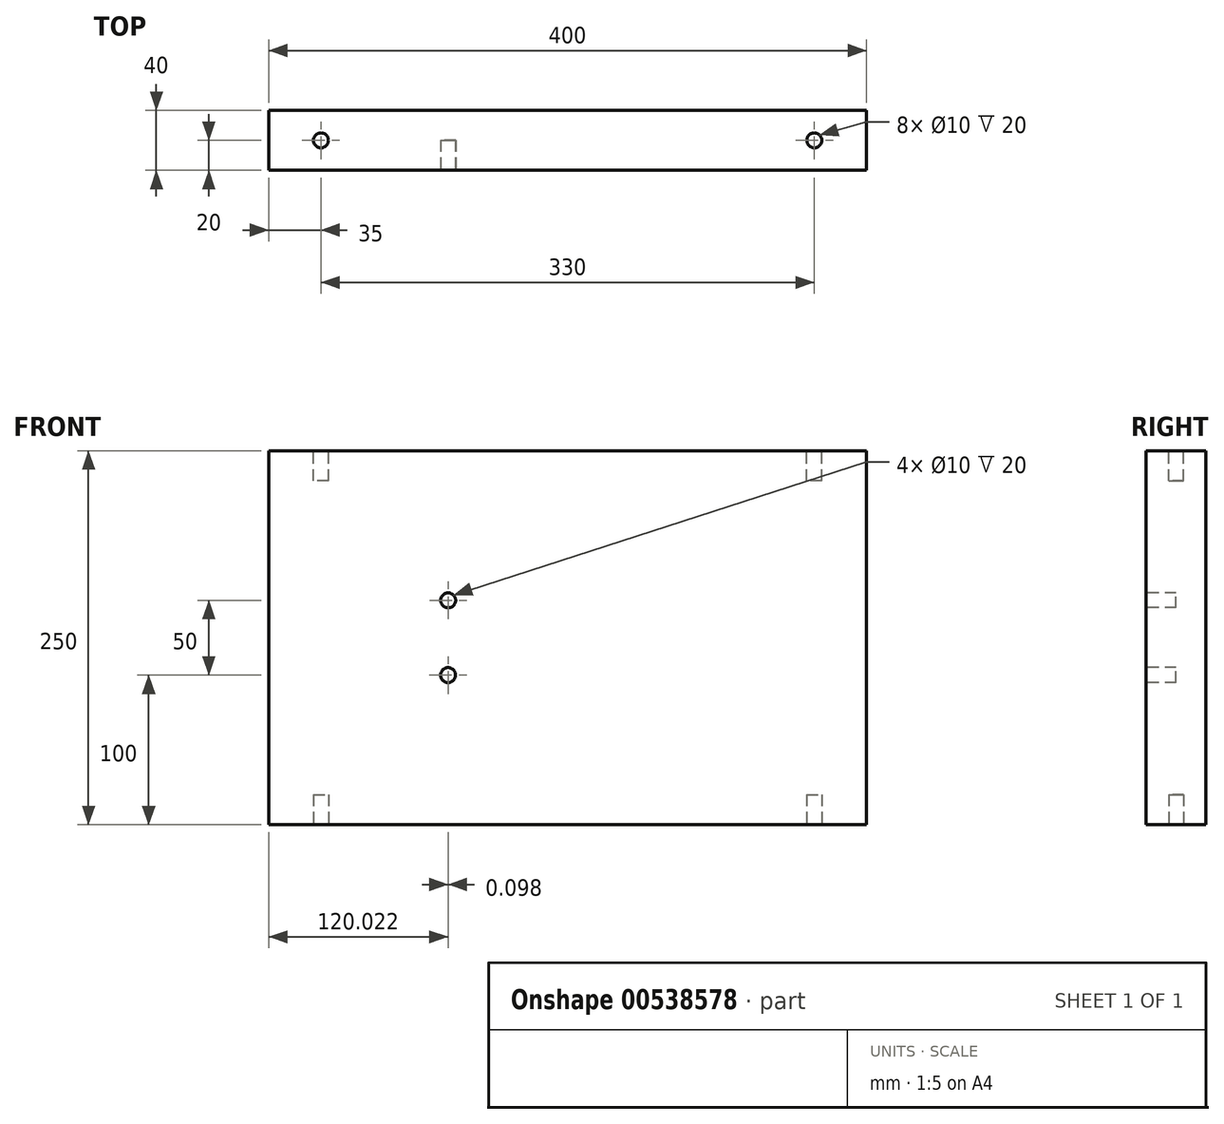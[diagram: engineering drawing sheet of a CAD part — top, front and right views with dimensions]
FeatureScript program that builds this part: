
annotation { "Feature Type Name" : "Feature", "Feature Type Description" : "" }
export const myFeature = defineFeature(function(context is Context, id is Id, definition is map)
    precondition{}
    {
        {
            var Q0;
            Q0=qCreatedBy(makeId("Right.planeOp"),FACE);
            var sketch = newSketch(context, id + "F0", { "sketchPlane" : qUnion([Q0])});
            skLineSegment(sketch, "E0.bottom", {"start": v(0, 0) * mm, "end": v(40, 0) * mm});
            skLineSegment(sketch, "E0.top", {"start": v(0, 250) * mm, "end": v(40, 250) * mm});
            skLineSegment(sketch, "E0.left", {"start": v(0, 0) * mm, "end": v(0, 250) * mm});
            skLineSegment(sketch, "E0.right", {"start": v(40, 0) * mm, "end": v(40, 250) * mm});
            skSolve(sketch);
        }
        {
            var Q0;
            Q0 = qSketchRegion(id + "F0", true);
            extrude(context, id + "F1", {"entities" : qUnion([Q0]), "endBound" : BoundingType.SYMMETRIC, "oppositeDirection" : true, "depth" : 400 * mm, "offsetDistance" : 25 * mm});
        }
        {
            var Q0;
            Q0=makeQuery(id+"F1.opExtrude","SWEPT_FACE",FACE,{"disambiguationData":[OSD([sQuery(id+"F0.wireOp",EDGE,"E0.left")])]});
            var sketch = newSketch(context, id + "F2", { "sketchPlane" : qUnion([Q0])});
            skLineSegment(sketch, "E1", {"start": v(-80, 250) * mm, "end": v(-80, 0) * mm, "construction": true});
            skSolve(sketch);
        }
        {
            var Q0;
            {var subQ0=sQuery(id+"F0.wireOp",EDGE,"E0.left");Q0=makeQuery(id+"F2.imprint","IMPRINT",FACE,{"disambiguationData":[TD([[makeQuery(id+"F2.imprint","IMPRINT",EDGE,{"derivedFrom":makeQuery(id+"F1.opExtrude","CAP_EDGE",EDGE,{"disambiguationData":[OSD([subQ0])],"isStart":true})}),1.0]])]});}
            var sketch = newSketch(context, id + "F3", { "sketchPlane" : qUnion([Q0])});
            skCircle(sketch, "E2", {"center": v(-79.88, 150) * mm, "radius": 5 * mm});
            skSolve(sketch);
        }
        {
            var Q0;
            {var subQ0=sQuery(id+"F0.wireOp",EDGE,"E0.left");Q0=makeQuery(id+"F2.imprint","IMPRINT",FACE,{"disambiguationData":[TD([[makeQuery(id+"F2.imprint","IMPRINT",EDGE,{"derivedFrom":makeQuery(id+"F1.opExtrude","CAP_EDGE",EDGE,{"disambiguationData":[OSD([subQ0])],"isStart":true})}),1.0]])]});}
            var sketch = newSketch(context, id + "F4", { "sketchPlane" : qUnion([Q0])});
            skCircle(sketch, "E3", {"center": v(-79.98, 100) * mm, "radius": 5 * mm});
            skSolve(sketch);
        }
        {
            var Q0;
            Q0=makeQuery(id+"F4.imprint","IMPRINT",FACE,{"disambiguationData":[TD([[makeQuery(id+"F4.imprint","IMPRINT",EDGE,{"derivedFrom":sQuery(id+"F4.wireOp",EDGE,"E3")}),1.0]])]});
            extrude(context, id + "F5", {"entities" : qUnion([Q0]), "operationType" : NewBodyOperationType.REMOVE, "oppositeDirection" : true, "depth" : 20 * mm, "offsetDistance" : 25 * mm});
        }
        {
            var Q0;
            Q0=makeQuery(id+"F3.imprint","IMPRINT",FACE,{"disambiguationData":[TD([[makeQuery(id+"F3.imprint","IMPRINT",EDGE,{"derivedFrom":sQuery(id+"F3.wireOp",EDGE,"E2")}),1.0]])]});
            extrude(context, id + "F6", {"entities" : qUnion([Q0]), "operationType" : NewBodyOperationType.REMOVE, "oppositeDirection" : true, "depth" : 20 * mm, "offsetDistance" : 25 * mm});
        }
        {
            var Q0;
            Q0=makeQuery(id+"F1.opExtrude","SWEPT_FACE",FACE,{"disambiguationData":[OSD([sQuery(id+"F0.wireOp",EDGE,"E0.top")])]});
            var sketch = newSketch(context, id + "F7", { "sketchPlane" : qUnion([Q0])});
            skCircle(sketch, "E4", {"center": v(-165, 20) * mm, "radius": 5 * mm});
            skSolve(sketch);
        }
        {
            var Q0;
            Q0=makeQuery(id+"F7.imprint","IMPRINT",FACE,{"disambiguationData":[TD([[makeQuery(id+"F7.imprint","IMPRINT",EDGE,{"derivedFrom":sQuery(id+"F7.wireOp",EDGE,"E4")}),1.0]])]});
            extrude(context, id + "F8", {"entities" : qUnion([Q0]), "operationType" : NewBodyOperationType.REMOVE, "oppositeDirection" : true, "depth" : 20 * mm, "offsetDistance" : 25 * mm});
        }
        {
            var Q0;
            Q0=makeQuery(id+"F1.opExtrude","SWEPT_FACE",FACE,{"disambiguationData":[OSD([sQuery(id+"F0.wireOp",EDGE,"E0.top")])]});
            var sketch = newSketch(context, id + "F9", { "sketchPlane" : qUnion([Q0])});
            skCircle(sketch, "E5", {"center": v(165, 20) * mm, "radius": 5 * mm});
            skSolve(sketch);
        }
        {
            var Q0;
            Q0=makeQuery(id+"F9.imprint","IMPRINT",FACE,{"disambiguationData":[TD([[makeQuery(id+"F9.imprint","IMPRINT",EDGE,{"derivedFrom":sQuery(id+"F9.wireOp",EDGE,"E5")}),1.0]])]});
            extrude(context, id + "F10", {"entities" : qUnion([Q0]), "operationType" : NewBodyOperationType.REMOVE, "oppositeDirection" : true, "depth" : 20 * mm, "offsetDistance" : 25 * mm});
        }
        {
            var Q0;
            Q0=makeQuery(id+"F1.opExtrude","SWEPT_FACE",FACE,{"disambiguationData":[OSD([sQuery(id+"F0.wireOp",EDGE,"E0.bottom")])]});
            var sketch = newSketch(context, id + "F11", { "sketchPlane" : qUnion([Q0])});
            skCircle(sketch, "E6", {"center": v(-165, -20) * mm, "radius": 5 * mm});
            skSolve(sketch);
        }
        {
            var Q0;
            Q0=makeQuery(id+"F11.imprint","IMPRINT",FACE,{"disambiguationData":[TD([[makeQuery(id+"F11.imprint","IMPRINT",EDGE,{"derivedFrom":sQuery(id+"F11.wireOp",EDGE,"E6")}),1.0]])]});
            extrude(context, id + "F12", {"entities" : qUnion([Q0]), "operationType" : NewBodyOperationType.REMOVE, "oppositeDirection" : true, "depth" : 20 * mm, "offsetDistance" : 25 * mm});
        }
        {
            var Q0;
            Q0=makeQuery(id+"F1.opExtrude","SWEPT_FACE",FACE,{"disambiguationData":[OSD([sQuery(id+"F0.wireOp",EDGE,"E0.bottom")])]});
            var sketch = newSketch(context, id + "F13", { "sketchPlane" : qUnion([Q0])});
            skCircle(sketch, "E7", {"center": v(165, -20) * mm, "radius": 5 * mm});
            skSolve(sketch);
        }
        {
            var Q0;
            Q0=makeQuery(id+"F13.imprint","IMPRINT",FACE,{"disambiguationData":[TD([[makeQuery(id+"F13.imprint","IMPRINT",EDGE,{"derivedFrom":sQuery(id+"F13.wireOp",EDGE,"E7")}),1.0]])]});
            extrude(context, id + "F14", {"entities" : qUnion([Q0]), "operationType" : NewBodyOperationType.REMOVE, "oppositeDirection" : true, "depth" : 20 * mm, "offsetDistance" : 25 * mm});
        }
    });
